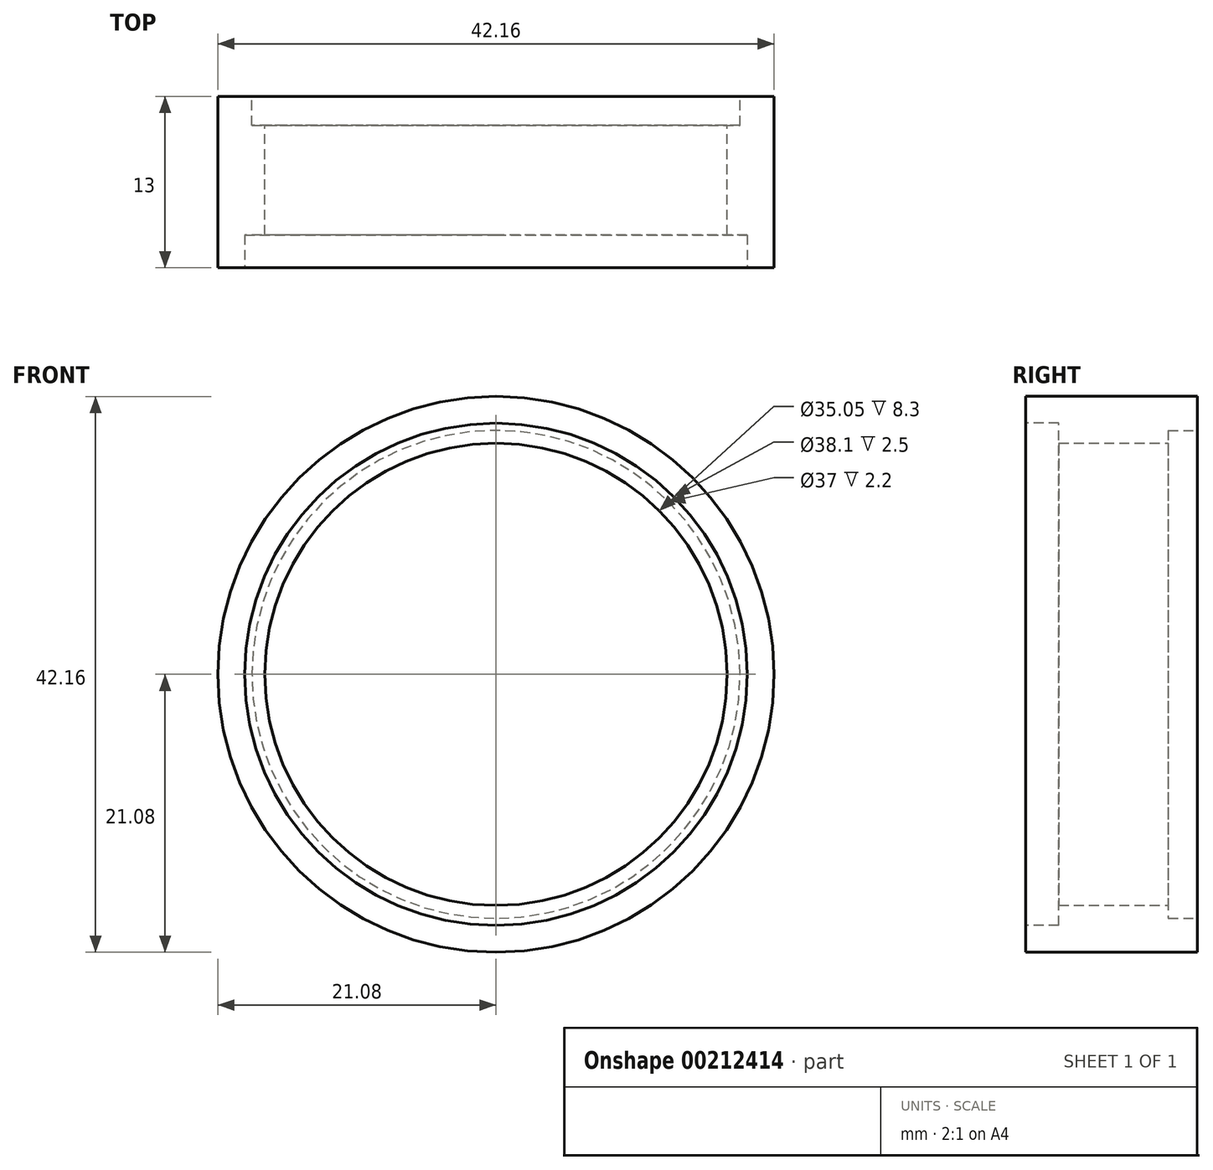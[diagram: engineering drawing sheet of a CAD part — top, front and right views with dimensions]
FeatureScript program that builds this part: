
annotation { "Feature Type Name" : "Feature", "Feature Type Description" : "" }
export const myFeature = defineFeature(function(context is Context, id is Id, definition is map)
    precondition{}
    {
        {
            var Q0;
            Q0=qCreatedBy(makeId("Front.planeOp"),FACE);
            var sketch = newSketch(context, id + "F0", { "sketchPlane" : qUnion([Q0])});
            skCircle(sketch, "E0", {"center": v(0, 0) * mm, "radius": 21.08 * mm});
            skCircle(sketch, "E1", {"center": v(0, 0) * mm, "radius": 17.53 * mm});
            skSolve(sketch);
        }
        {
            var Q0;
            Q0=qSketchRegion(id+"F0",true);
            extrude(context, id + "F1", {"entities" : qUnion([Q0]), "depth" : 13 * mm});
        }
        {
            var Q0;
            Q0=makeQuery(id+"F1.opExtrude","CAP_FACE",FACE,{"disambiguationData":[OSD([sQuery(id+"F0.wireOp",EDGE,"E0"),sQuery(id+"F0.wireOp",EDGE,"E1")])],"isStart":false});
            var sketch = newSketch(context, id + "F2", { "sketchPlane" : qUnion([Q0])});
            skCircle(sketch, "E2", {"center": v(0, 0) * mm, "radius": 19.05 * mm});
            skSolve(sketch);
        }
        {
            var Q0;
            Q0 = qSketchRegion(id + "F2", true);
            extrude(context, id + "F3", {"entities" : qUnion([Q0]), "operationType" : NewBodyOperationType.REMOVE, "oppositeDirection" : true, "depth" : 2.5 * mm});
        }
        {
            var Q0;
            Q0=makeQuery(id+"F1.opExtrude","CAP_FACE",FACE,{"disambiguationData":[OSD([sQuery(id+"F0.wireOp",EDGE,"E0"),sQuery(id+"F0.wireOp",EDGE,"E1")])],"isStart":true});
            var sketch = newSketch(context, id + "F4", { "sketchPlane" : qUnion([Q0])});
            skCircle(sketch, "E3", {"center": v(0, 0) * mm, "radius": 18.5 * mm});
            skSolve(sketch);
        }
        {
            var Q0;
            Q0 = qSketchRegion(id + "F4", true);
            extrude(context, id + "F5", {"entities" : qUnion([Q0]), "operationType" : NewBodyOperationType.REMOVE, "oppositeDirection" : true, "depth" : 2.2 * mm});
        }
    });
